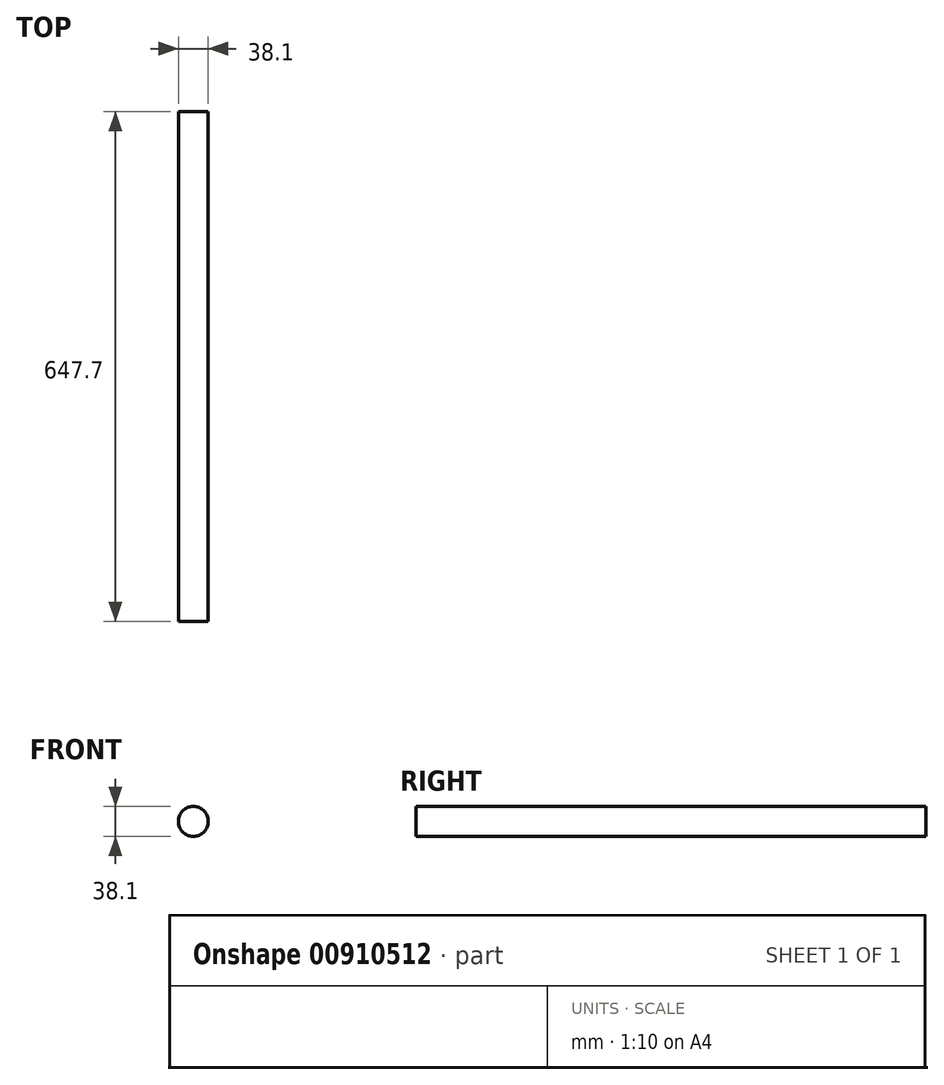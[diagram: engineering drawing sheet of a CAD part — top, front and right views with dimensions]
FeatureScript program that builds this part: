
annotation { "Feature Type Name" : "Feature", "Feature Type Description" : "" }
export const myFeature = defineFeature(function(context is Context, id is Id, definition is map)
    precondition{}
    {
        {
            var Q0;
            Q0=qCreatedBy(makeId("Top.planeOp"),FACE);
            var sketch = newSketch(context, id + "F0", { "sketchPlane" : qUnion([Q0])});
            skLineSegment(sketch, "E0", {"start": v(-51.3, 622.13) * mm, "end": v(-32.26, 622.13) * mm});
            skLineSegment(sketch, "E1", {"start": v(-32.26, 622.13) * mm, "end": v(-32.26, -25.57) * mm});
            skLineSegment(sketch, "E2", {"start": v(-32.26, -25.57) * mm, "end": v(-51.3, -25.57) * mm});
            skLineSegment(sketch, "E3", {"start": v(-51.3, -25.57) * mm, "end": v(-51.3, 622.13) * mm});
            skSolve(sketch);
        }
        {
            var Q0;
            Q0=makeQuery(id+"F0.imprint","IMPRINT",FACE,{"disambiguationData":[TD([[makeQuery(id+"F0.imprint","IMPRINT",EDGE,{"derivedFrom":sQuery(id+"F0.wireOp",EDGE,"E0")}),-1.0]])]});
            var Q1;
            Q1=sQuery(id+"F0.wireOp",EDGE,"E3");
            revolve(context, id + "F1", {"surfaceOperationType" : NewSurfaceOperationType.NEW, "entities" : qUnion([Q0]), "axis" : qUnion([Q1]), "revolveType" : RevolveType.FULL});
        }
    });
